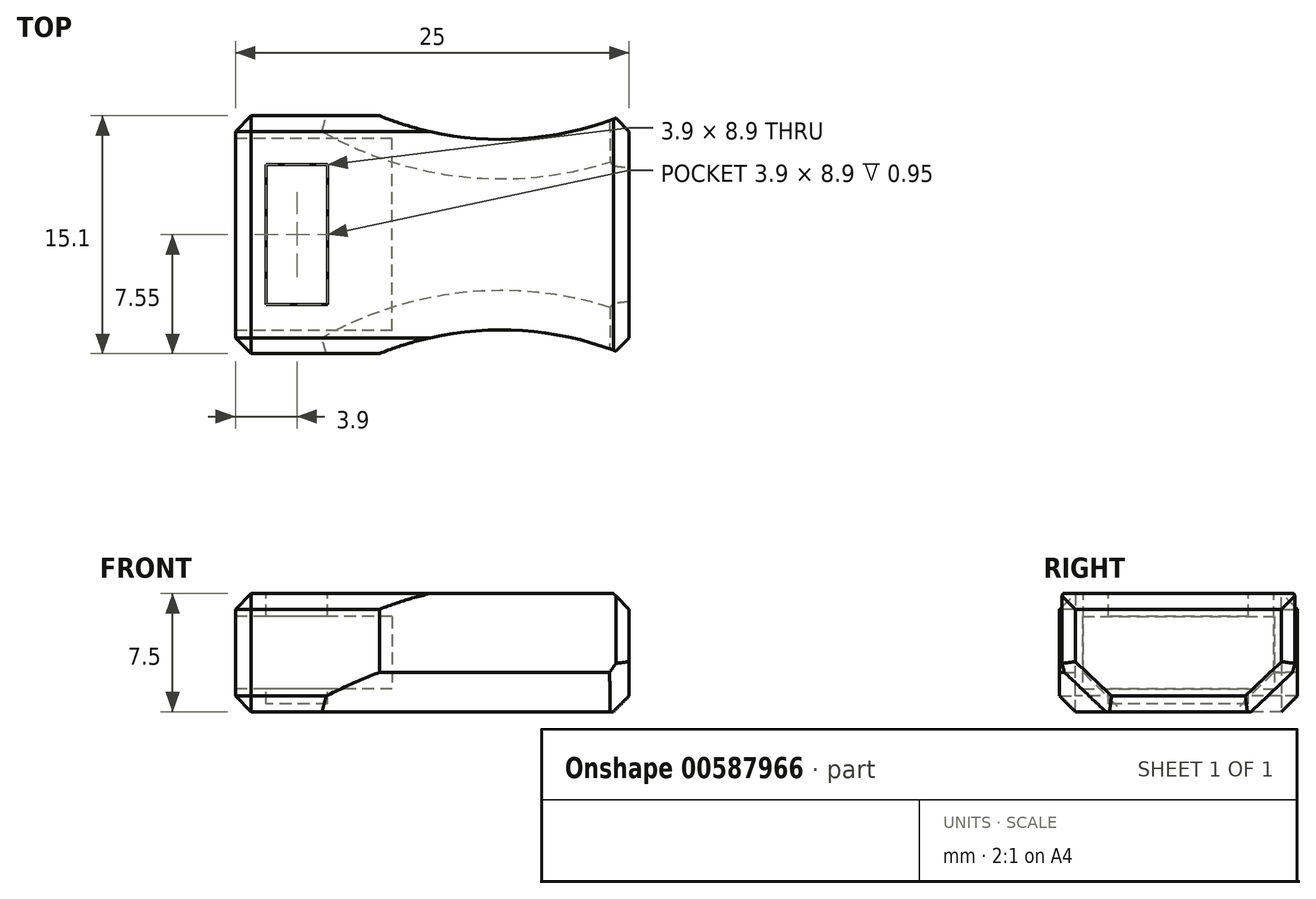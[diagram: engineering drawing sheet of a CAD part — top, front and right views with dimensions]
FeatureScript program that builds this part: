
annotation { "Feature Type Name" : "Feature", "Feature Type Description" : "" }
export const myFeature = defineFeature(function(context is Context, id is Id, definition is map)
    precondition{}
    {
        {
            var Q0;
            Q0=qCreatedBy(makeId("Top.planeOp"),FACE);
            var sketch = newSketch(context, id + "F0", { "sketchPlane" : qUnion([Q0])});
            skLineSegment(sketch, "E0.bottom", {"start": v(25, 7.55) * mm, "end": v(0, 7.55) * mm});
            skLineSegment(sketch, "E0.top", {"start": v(25, -7.55) * mm, "end": v(0, -7.55) * mm});
            skLineSegment(sketch, "E0.left", {"start": v(25, 7.55) * mm, "end": v(25, -7.55) * mm});
            skLineSegment(sketch, "E0.right", {"start": v(0, 7.55) * mm, "end": v(0, -7.55) * mm});
            skPoint(sketch, "E0.middle", {"position": v(0, 0) * mm});
            skSolve(sketch);
        }
        {
            var Q0;
            Q0=qSketchRegion(id+"F0",true);
            extrude(context, id + "F1", {"entities" : qUnion([Q0]), "depth" : 7.5 * mm, "offsetDistance" : 25 * mm});
        }
        {
            var Q0;
            Q0=makeQuery(id+"F1.opExtrude","SWEPT_FACE",FACE,{"disambiguationData":[OSD([sQuery(id+"F0.wireOp",EDGE,"E0.right")])]});
            var sketch = newSketch(context, id + "F2", { "sketchPlane" : qUnion([Q0])});
            skLineSegment(sketch, "E1.bottom", {"start": v(6.1, 6.05) * mm, "end": v(-6.1, 6.05) * mm});
            skLineSegment(sketch, "E1.top", {"start": v(6.1, 1.45) * mm, "end": v(-6.1, 1.45) * mm});
            skLineSegment(sketch, "E1.left", {"start": v(6.1, 6.05) * mm, "end": v(6.1, 1.45) * mm});
            skLineSegment(sketch, "E1.right", {"start": v(-6.1, 6.05) * mm, "end": v(-6.1, 1.45) * mm});
            skPoint(sketch, "E1.middle", {"position": v(0, 3.75) * mm});
            skSolve(sketch);
        }
        {
            var Q0;
            Q0=qSketchRegion(id+"F2",true);
            extrude(context, id + "F3", {"entities" : qUnion([Q0]), "operationType" : NewBodyOperationType.REMOVE, "oppositeDirection" : true, "depth" : 9.95 * mm, "offsetDistance" : 25 * mm});
        }
        {
            var Q0;
            Q0=makeQuery(id+"F1.opExtrude","CAP_FACE",FACE,{"disambiguationData":[OSD([sQuery(id+"F0.wireOp",EDGE,"E0.bottom"),sQuery(id+"F0.wireOp",EDGE,"E0.top"),sQuery(id+"F0.wireOp",EDGE,"E0.left"),sQuery(id+"F0.wireOp",EDGE,"E0.right")])],"isStart":false});
            var sketch = newSketch(context, id + "F4", { "sketchPlane" : qUnion([Q0])});
            skLineSegment(sketch, "E2.bottom", {"start": v(5.85, 4.45) * mm, "end": v(1.95, 4.45) * mm});
            skLineSegment(sketch, "E2.top", {"start": v(5.85, -4.45) * mm, "end": v(1.95, -4.45) * mm});
            skLineSegment(sketch, "E2.left", {"start": v(5.85, 4.45) * mm, "end": v(5.85, -4.45) * mm});
            skLineSegment(sketch, "E2.right", {"start": v(1.95, 4.45) * mm, "end": v(1.95, -4.45) * mm});
            skPoint(sketch, "E2.middle", {"position": v(3.9, 0) * mm});
            skSolve(sketch);
        }
        {
            var Q0;
            Q0=qSketchRegion(id+"F4",true);
            extrude(context, id + "F5", {"entities" : qUnion([Q0]), "operationType" : NewBodyOperationType.REMOVE, "oppositeDirection" : true, "depth" : 25 * mm, "offsetDistance" : 25 * mm});
        }
        {
            var Q0;
            Q0=makeQuery(id+"F1.opExtrude","CAP_FACE",FACE,{"disambiguationData":[OSD([sQuery(id+"F0.wireOp",EDGE,"E0.bottom"),sQuery(id+"F0.wireOp",EDGE,"E0.top"),sQuery(id+"F0.wireOp",EDGE,"E0.left"),sQuery(id+"F0.wireOp",EDGE,"E0.right")])],"isStart":false});
            var sketch = newSketch(context, id + "F6", { "sketchPlane" : qUnion([Q0])});
            skCircle(sketch, "E3", {"center": v(16.85, 26.55) * mm, "radius": 20.5 * mm});
            skCircle(sketch, "E4", {"center": v(16.85, -26.55) * mm, "radius": 20.5 * mm});
            skSolve(sketch);
        }
        {
            var Q0;
            Q0=qSketchRegion(id+"F6",true);
            extrude(context, id + "F7", {"entities" : qUnion([Q0]), "operationType" : NewBodyOperationType.REMOVE, "oppositeDirection" : true, "depth" : 25 * mm, "offsetDistance" : 25 * mm});
        }
        {
            var Q0;
            Q0=makeQuery(id+"F1.opExtrude","CAP_FACE",FACE,{"disambiguationData":[OSD([sQuery(id+"F0.wireOp",EDGE,"E0.bottom"),sQuery(id+"F0.wireOp",EDGE,"E0.top"),sQuery(id+"F0.wireOp",EDGE,"E0.left"),sQuery(id+"F0.wireOp",EDGE,"E0.right")])],"isStart":true});
            var sketch = newSketch(context, id + "F8", { "sketchPlane" : qUnion([Q0])});
            skLineSegment(sketch, "E5.bottom", {"start": v(1.46, 4.94) * mm, "end": v(8.37, 4.94) * mm});
            skLineSegment(sketch, "E5.top", {"start": v(1.46, -5) * mm, "end": v(8.37, -5) * mm});
            skLineSegment(sketch, "E5.left", {"start": v(1.46, 4.94) * mm, "end": v(1.46, -5) * mm});
            skLineSegment(sketch, "E5.right", {"start": v(8.37, 4.94) * mm, "end": v(8.37, -5) * mm});
            skSolve(sketch);
        }
        {
            var Q0;
            Q0=qSketchRegion(id+"F8",true);
            extrude(context, id + "F9", {"entities" : qUnion([Q0]), "operationType" : NewBodyOperationType.ADD, "oppositeDirection" : true, "depth" : .5 * mm, "offsetDistance" : 25 * mm});
        }
        {
            var Q0;
            Q0=makeQuery(id+"F7.boolean.opBoolean","COPY",EDGE,{"derivedFrom":makeQuery(id+"F7.opExtrude","CAP_EDGE",EDGE,{"disambiguationData":[OSD([sQuery(id+"F6.wireOp",EDGE,"E4")])],"isStart":true})});
            var Q1;
            Q1=makeQuery(id+"F7.boolean.opBoolean","COPY",EDGE,{"derivedFrom":makeQuery(id+"F7.opExtrude","CAP_EDGE",EDGE,{"disambiguationData":[OSD([sQuery(id+"F6.wireOp",EDGE,"E3")])],"isStart":true})});
            var Q2;
            Q2=makeQuery(id+"F7.boolean.opBoolean","INTERSECT",EDGE,{"derivedFrom":[makeQuery(id+"F1.opExtrude","CAP_FACE",FACE,{"disambiguationData":[OSD([sQuery(id+"F0.wireOp",EDGE,"E0.bottom"),sQuery(id+"F0.wireOp",EDGE,"E0.top"),sQuery(id+"F0.wireOp",EDGE,"E0.left"),sQuery(id+"F0.wireOp",EDGE,"E0.right")])],"isStart":true}),makeQuery(id+"F7.opExtrude","SWEPT_FACE",FACE,{"disambiguationData":[OSD([sQuery(id+"F6.wireOp",EDGE,"E4")])]})]});
            var Q3;
            Q3=makeQuery(id+"F7.boolean.opBoolean","INTERSECT",EDGE,{"derivedFrom":[makeQuery(id+"F1.opExtrude","CAP_FACE",FACE,{"disambiguationData":[OSD([sQuery(id+"F0.wireOp",EDGE,"E0.bottom"),sQuery(id+"F0.wireOp",EDGE,"E0.top"),sQuery(id+"F0.wireOp",EDGE,"E0.left"),sQuery(id+"F0.wireOp",EDGE,"E0.right")])],"isStart":true}),makeQuery(id+"F7.opExtrude","SWEPT_FACE",FACE,{"disambiguationData":[OSD([sQuery(id+"F6.wireOp",EDGE,"E3")])]})]});
            chamfer(context, id + "F10", {"entities" : qUnion([Q0, Q1, Q2, Q3]), "width" : 2.5 * mm, "tangentPropagation" : true});
        }
        {
            var Q0;
            Q0=makeQuery(id+"F1.opExtrude","SWEPT_FACE",FACE,{"disambiguationData":[OSD([sQuery(id+"F0.wireOp",EDGE,"E0.left")])]});
            var Q1;
            Q1=makeQuery(id+"F1.opExtrude","SWEPT_EDGE",EDGE,{"disambiguationData":[OSD([sQuery(id+"F0.wireOp",EDGE,"E0.bottom"),sQuery(id+"F0.wireOp",EDGE,"E0.right")])]});
            var Q2;
            Q2=makeQuery(id+"F1.opExtrude","CAP_EDGE",EDGE,{"disambiguationData":[OSD([sQuery(id+"F0.wireOp",EDGE,"E0.right")])],"isStart":false});
            var Q3;
            Q3=makeQuery(id+"F1.opExtrude","CAP_EDGE",EDGE,{"disambiguationData":[OSD([sQuery(id+"F0.wireOp",EDGE,"E0.right")])],"isStart":true});
            var Q4;
            Q4=makeQuery(id+"F1.opExtrude","SWEPT_EDGE",EDGE,{"disambiguationData":[OSD([sQuery(id+"F0.wireOp",EDGE,"E0.top"),sQuery(id+"F0.wireOp",EDGE,"E0.right")])]});
            var Q5;
            {var subQ0=sQuery(id+"F0.wireOp",EDGE,"E0.right");var subQ1=sQuery(id+"F0.wireOp",EDGE,"E0.top");Q5=makeQuery(id+"F7.boolean.opBoolean","SPLIT",EDGE,{"disambiguationData":[TD([makeQuery(id+"F1.opExtrude","SWEPT_FACE",FACE,{"disambiguationData":[OSD([subQ0])]})])],"derivedFrom":makeQuery(id+"F1.opExtrude","CAP_EDGE",EDGE,{"disambiguationData":[OSD([subQ1])],"isStart":false})});}
            var Q6;
            {var subQ0=sQuery(id+"F0.wireOp",EDGE,"E0.bottom");var subQ1=sQuery(id+"F0.wireOp",EDGE,"E0.right");Q6=makeQuery(id+"F7.boolean.opBoolean","SPLIT",EDGE,{"disambiguationData":[TD([makeQuery(id+"F1.opExtrude","SWEPT_FACE",FACE,{"disambiguationData":[OSD([subQ1])]})])],"derivedFrom":makeQuery(id+"F1.opExtrude","CAP_EDGE",EDGE,{"disambiguationData":[OSD([subQ0])],"isStart":false})});}
            var Q7;
            {var subQ0=sQuery(id+"F0.wireOp",EDGE,"E0.right");var subQ1=sQuery(id+"F0.wireOp",EDGE,"E0.top");Q7=makeQuery(id+"F7.boolean.opBoolean","SPLIT",EDGE,{"disambiguationData":[TD([makeQuery(id+"F1.opExtrude","SWEPT_FACE",FACE,{"disambiguationData":[OSD([subQ0])]})])],"derivedFrom":makeQuery(id+"F1.opExtrude","CAP_EDGE",EDGE,{"disambiguationData":[OSD([subQ1])],"isStart":true})});}
            var Q8;
            {var subQ0=sQuery(id+"F0.wireOp",EDGE,"E0.bottom");var subQ1=sQuery(id+"F0.wireOp",EDGE,"E0.right");Q8=makeQuery(id+"F7.boolean.opBoolean","SPLIT",EDGE,{"disambiguationData":[TD([makeQuery(id+"F1.opExtrude","SWEPT_FACE",FACE,{"disambiguationData":[OSD([subQ1])]})])],"derivedFrom":makeQuery(id+"F1.opExtrude","CAP_EDGE",EDGE,{"disambiguationData":[OSD([subQ0])],"isStart":true})});}
            chamfer(context, id + "F11", {"entities" : qUnion([Q0, Q1, Q2, Q3, Q4, Q5, Q6, Q7, Q8]), "width" : 1 * mm, "tangentPropagation" : true});
        }
    });
